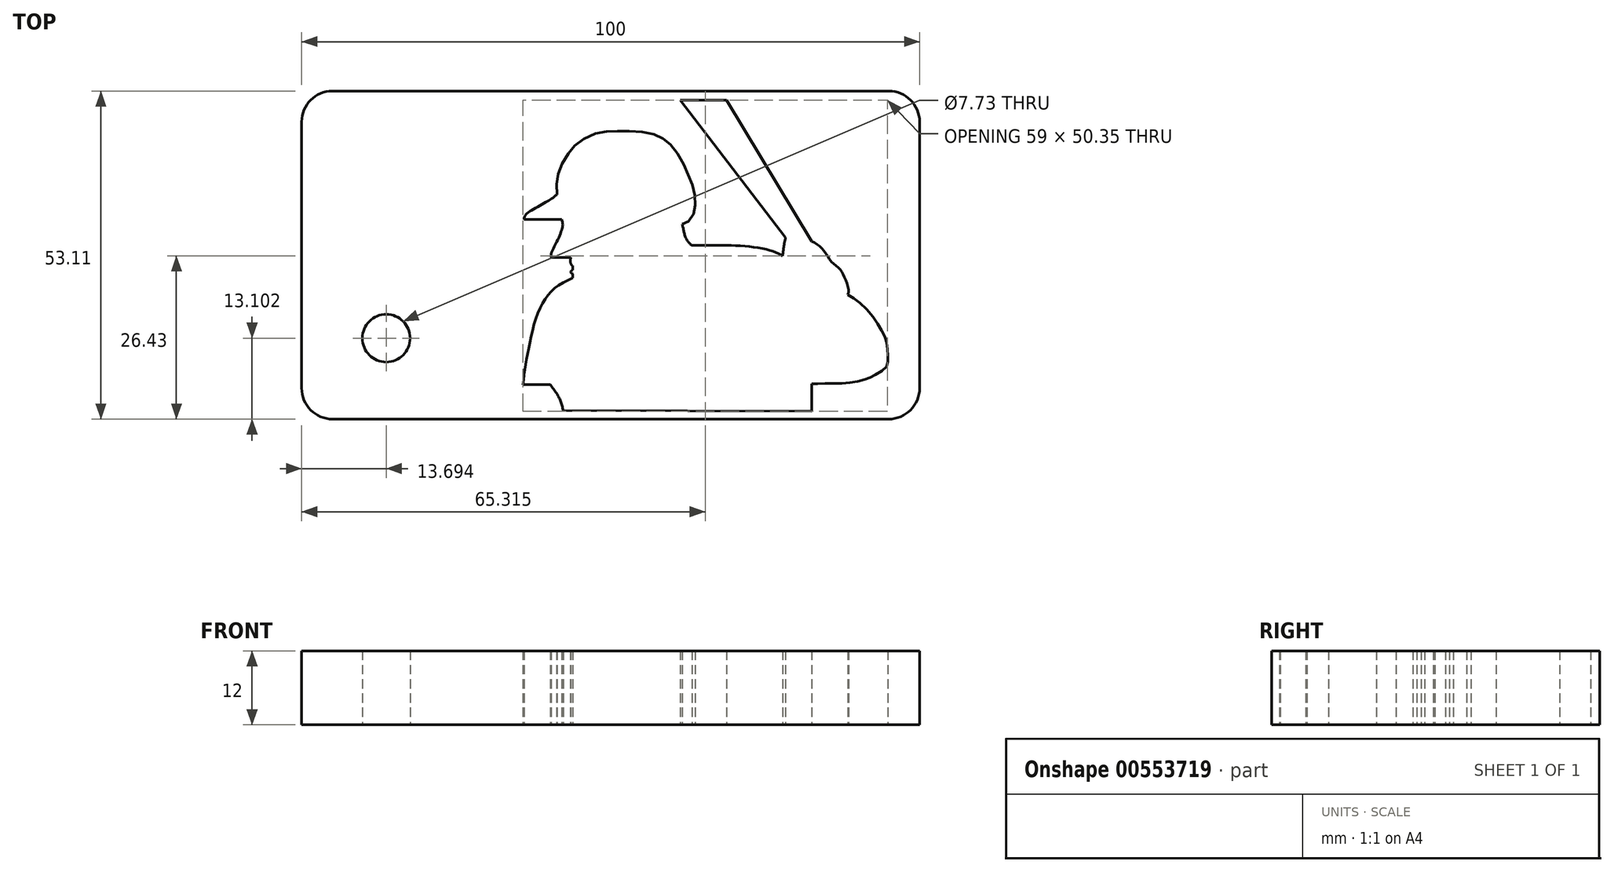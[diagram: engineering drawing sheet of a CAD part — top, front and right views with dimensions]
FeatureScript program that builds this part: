
annotation { "Feature Type Name" : "Feature", "Feature Type Description" : "" }
export const myFeature = defineFeature(function(context is Context, id is Id, definition is map)
    precondition{}
    {
        {
            var Q0;
            Q0=qCreatedBy(makeId("Top.planeOp"),FACE);
            var sketch = newSketch(context, id + "F0", { "sketchPlane" : qUnion([Q0])});
            skLineSegment(sketch, "E0", {"start": v(50, 53.11) * mm, "end": v(50, 0) * mm, "construction": true});
            skLineSegment(sketch, "E1", {"start": v(0, 26.56) * mm, "end": v(100, 26.56) * mm, "construction": true});
            skLineSegment(sketch, "E2.bottom", {"start": v(100, 0) * mm, "end": v(0, 0) * mm});
            skLineSegment(sketch, "E2.top", {"start": v(100, 53.11) * mm, "end": v(0, 53.11) * mm});
            skLineSegment(sketch, "E2.left", {"start": v(100, 0) * mm, "end": v(100, 53.11) * mm});
            skLineSegment(sketch, "E2.right", {"start": v(0, 0) * mm, "end": v(0, 53.11) * mm});
            skPoint(sketch, "E2.middle", {"position": v(50, 26.56) * mm});
            skSolve(sketch);
        }
        {
            var Q0;
            Q0 = qSketchRegion(id + "F0", true);
            extrude(context, id + "F1", {"entities" : qUnion([Q0]), "depth" : 12 * mm, "offsetDistance" : 25 * mm});
        }
        {
            var Q0;
            Q0=qCreatedBy(makeId("Top.planeOp"),FACE);
            var sketch = newSketch(context, id + "F2", { "sketchPlane" : qUnion([Q0])});
            skCircle(sketch, "E3", {"center": v(13.7, 13.1) * mm, "radius": 3.87 * mm});
            skFitSpline(sketch, "E4", {"points": [v(42.35, 1.42) * mm, v(41.67, 3.45) * mm, v(40.23, 5.56) * mm], "startDerivative": vector(-1.11, 4.28) * mm, "endDerivative": vector(-3.09, 4) * mm});
            skLineSegment(sketch, "E5", {"start": v(40.23, 5.56) * mm, "end": v(35.82, 5.56) * mm});
            skFitSpline(sketch, "E6", {"points": [v(35.82, 5.56) * mm, v(36.2, 8.52) * mm, v(36.85, 11.97) * mm, v(37.88, 16.2) * mm, v(39.36, 19.3) * mm, v(41.13, 21.32) * mm, v(43.9, 22.85) * mm], "startDerivative": vector(2.06, 18.6) * mm, "endDerivative": vector(18.38, 8.52) * mm});
            skFitSpline(sketch, "E7", {"points": [v(43.9, 22.85) * mm, v(43.9, 23.49) * mm], "startDerivative": vector(0, 0.63) * mm, "endDerivative": vector(0, 0.63) * mm});
            skFitSpline(sketch, "E8", {"points": [v(43.9, 23.49) * mm, v(43.52, 23.8) * mm, v(43.9, 24.19) * mm], "startDerivative": vector(-1.14, 0.6) * mm, "endDerivative": vector(1.12, 0.81) * mm});
            skFitSpline(sketch, "E9", {"points": [v(43.9, 24.19) * mm, v(43.9, 24.78) * mm], "startDerivative": vector(0, 0.59) * mm, "endDerivative": vector(0, 0.59) * mm});
            skFitSpline(sketch, "E10", {"points": [v(43.9, 24.78) * mm, v(43.57, 25.13) * mm, v(43.55, 26.16) * mm], "startDerivative": vector(-0.97, 0.7) * mm, "endDerivative": vector(0.19, 2) * mm});
            skLineSegment(sketch, "E11", {"start": v(43.55, 26.16) * mm, "end": v(40.4, 26.16) * mm});
            skFitSpline(sketch, "E12", {"points": [v(40.4, 26.16) * mm, v(40.4, 26.75) * mm, v(41.4, 28.94) * mm, v(42.11, 30.7) * mm, v(42.25, 31.5) * mm, v(42.07, 32.3) * mm], "startDerivative": vector(-0.67, 3.57) * mm, "endDerivative": vector(-1.59, 4.94) * mm});
            skLineSegment(sketch, "E13", {"start": v(42.07, 32.3) * mm, "end": v(35.98, 32.3) * mm});
            skFitSpline(sketch, "E14", {"points": [v(35.98, 32.3) * mm, v(36.22, 33.02) * mm, v(37.2, 33.8) * mm, v(39.18, 34.93) * mm, v(40.4, 35.63) * mm, v(41.31, 36.34) * mm], "startDerivative": vector(0.88, 5.02) * mm, "endDerivative": vector(4.78, 3.93) * mm});
            skFitSpline(sketch, "E15", {"points": [v(41.31, 36.34) * mm, v(41.31, 38.64) * mm, v(41.9, 40.82) * mm, v(43.33, 43.24) * mm, v(44.84, 44.82) * mm, v(47.68, 46.25) * mm, v(50.26, 46.58) * mm, v(52.99, 46.63) * mm, v(56.26, 46.27) * mm, v(58.42, 45.48) * mm, v(59.87, 44.25) * mm, v(61.56, 41.7) * mm, v(62.67, 39.32) * mm, v(63.5, 36.97) * mm, v(63.68, 34.8) * mm, v(63.44, 33.19) * mm, v(62.48, 31.92) * mm, v(61.61, 31.54) * mm], "startDerivative": vector(-1.9, 39.86) * mm, "endDerivative": vector(-23.05, -6.57) * mm});
            skFitSpline(sketch, "E16", {"points": [v(61.61, 31.54) * mm, v(61.82, 30.49) * mm, v(62.13, 29.43) * mm, v(62.72, 28.49) * mm, v(63.16, 28.11) * mm], "startDerivative": vector(0.78, -3.99) * mm, "endDerivative": vector(2.25, -1.6) * mm});
            skFitSpline(sketch, "E17", {"points": [v(63.16, 28.11) * mm, v(65.7, 28.11) * mm, v(69.15, 28.11) * mm, v(72.51, 27.9) * mm, v(75.33, 27.43) * mm, v(76.93, 26.9) * mm, v(77.85, 26.42) * mm], "startDerivative": vector(14.18, -0.05) * mm, "endDerivative": vector(7.88, -4.35) * mm});
            skFitSpline(sketch, "E18", {"points": [v(77.85, 26.42) * mm, v(78.01, 27.83) * mm, v(78.32, 29.43) * mm], "startDerivative": vector(0.28, 2.88) * mm, "endDerivative": vector(0.66, 3.13) * mm});
            skFitSpline(sketch, "E19", {"points": [v(78.32, 29.43) * mm, v(61.26, 51.6) * mm], "startDerivative": vector(-17.06, 22.18) * mm, "endDerivative": vector(-17.06, 22.18) * mm});
            skLineSegment(sketch, "E20", {"start": v(61.26, 51.6) * mm, "end": v(68.75, 51.6) * mm});
            skFitSpline(sketch, "E21", {"points": [v(68.75, 51.6) * mm, v(82.56, 28.8) * mm], "startDerivative": vector(13.8, -22.82) * mm, "endDerivative": vector(13.8, -22.82) * mm});
            skFitSpline(sketch, "E22", {"points": [v(82.56, 28.8) * mm, v(84.29, 27.56) * mm, v(85.63, 25.6) * mm, v(87.08, 24.27) * mm, v(87.98, 22.64) * mm, v(88.53, 20.63) * mm, v(88.37, 20.13) * mm], "startDerivative": vector(10.24, -5.6) * mm, "endDerivative": vector(-2.67, -4.41) * mm});
            skFitSpline(sketch, "E23", {"points": [v(88.37, 20.13) * mm, v(90.24, 18.88) * mm, v(92.58, 16.39) * mm, v(93.93, 14.2) * mm, v(94.61, 12.6) * mm, v(94.83, 10.79) * mm, v(94.88, 9.36) * mm, v(94.48, 8.3) * mm, v(92.72, 7.09) * mm, v(91.62, 6.57) * mm, v(89.54, 6) * mm, v(86.99, 5.79) * mm, v(84.15, 5.74) * mm, v(82.56, 5.7) * mm], "startDerivative": vector(22.51, -13.17) * mm, "endDerivative": vector(-21.36, -0.51) * mm});
            skFitSpline(sketch, "E24", {"points": [v(82.56, 5.7) * mm, v(82.56, 1.25) * mm], "startDerivative": vector(0, -4.45) * mm, "endDerivative": vector(0, -4.45) * mm});
            skLineSegment(sketch, "E25", {"start": v(42.35, 1.42) * mm, "end": v(82.56, 1.25) * mm});
            skSolve(sketch);
        }
        {
            var Q0;
            Q0 = qSketchRegion(id + "F2", true);
            var Q1;
            Q1=makeQuery(id+"F1.opExtrude","CAP_FACE",FACE,{"disambiguationData":[OSD([sQuery(id+"F0.wireOp",EDGE,"E2.bottom"),sQuery(id+"F0.wireOp",EDGE,"E2.top"),sQuery(id+"F0.wireOp",EDGE,"E2.left"),sQuery(id+"F0.wireOp",EDGE,"E2.right")])],"isStart":false});
            var Q2;
            Q2=makeQuery(id+"F1.opExtrude","CAP_FACE",FACE,{"disambiguationData":[OSD([sQuery(id+"F0.wireOp",EDGE,"E2.bottom"),sQuery(id+"F0.wireOp",EDGE,"E2.top"),sQuery(id+"F0.wireOp",EDGE,"E2.left"),sQuery(id+"F0.wireOp",EDGE,"E2.right")])],"isStart":false});
            extrude(context, id + "F3", {"entities" : qUnion([Q0, Q1, Q2]), "operationType" : NewBodyOperationType.REMOVE, "depth" : 14.9 * mm, "offsetDistance" : 25 * mm});
        }
        {
            var Q0;
            Q0=makeQuery(id+"F1.opExtrude","SWEPT_EDGE",EDGE,{"disambiguationData":[OSD([sQuery(id+"F0.wireOp",EDGE,"E2.top"),sQuery(id+"F0.wireOp",EDGE,"E2.right")])]});
            var Q1;
            Q1=makeQuery(id+"F1.opExtrude","SWEPT_EDGE",EDGE,{"disambiguationData":[OSD([sQuery(id+"F0.wireOp",EDGE,"E2.bottom"),sQuery(id+"F0.wireOp",EDGE,"E2.right")])]});
            var Q2;
            Q2=makeQuery(id+"F1.opExtrude","SWEPT_EDGE",EDGE,{"disambiguationData":[OSD([sQuery(id+"F0.wireOp",EDGE,"E2.top"),sQuery(id+"F0.wireOp",EDGE,"E2.left")])]});
            var Q3;
            Q3=makeQuery(id+"F1.opExtrude","SWEPT_EDGE",EDGE,{"disambiguationData":[OSD([sQuery(id+"F0.wireOp",EDGE,"E2.bottom"),sQuery(id+"F0.wireOp",EDGE,"E2.left")])]});
            fillet(context, id + "F4", {"entities" : qUnion([Q0, Q1, Q2, Q3]), "radius" : 5 * mm, "tangentPropagation" : true, "allowEdgeOverflow" : false});
        }
    });
